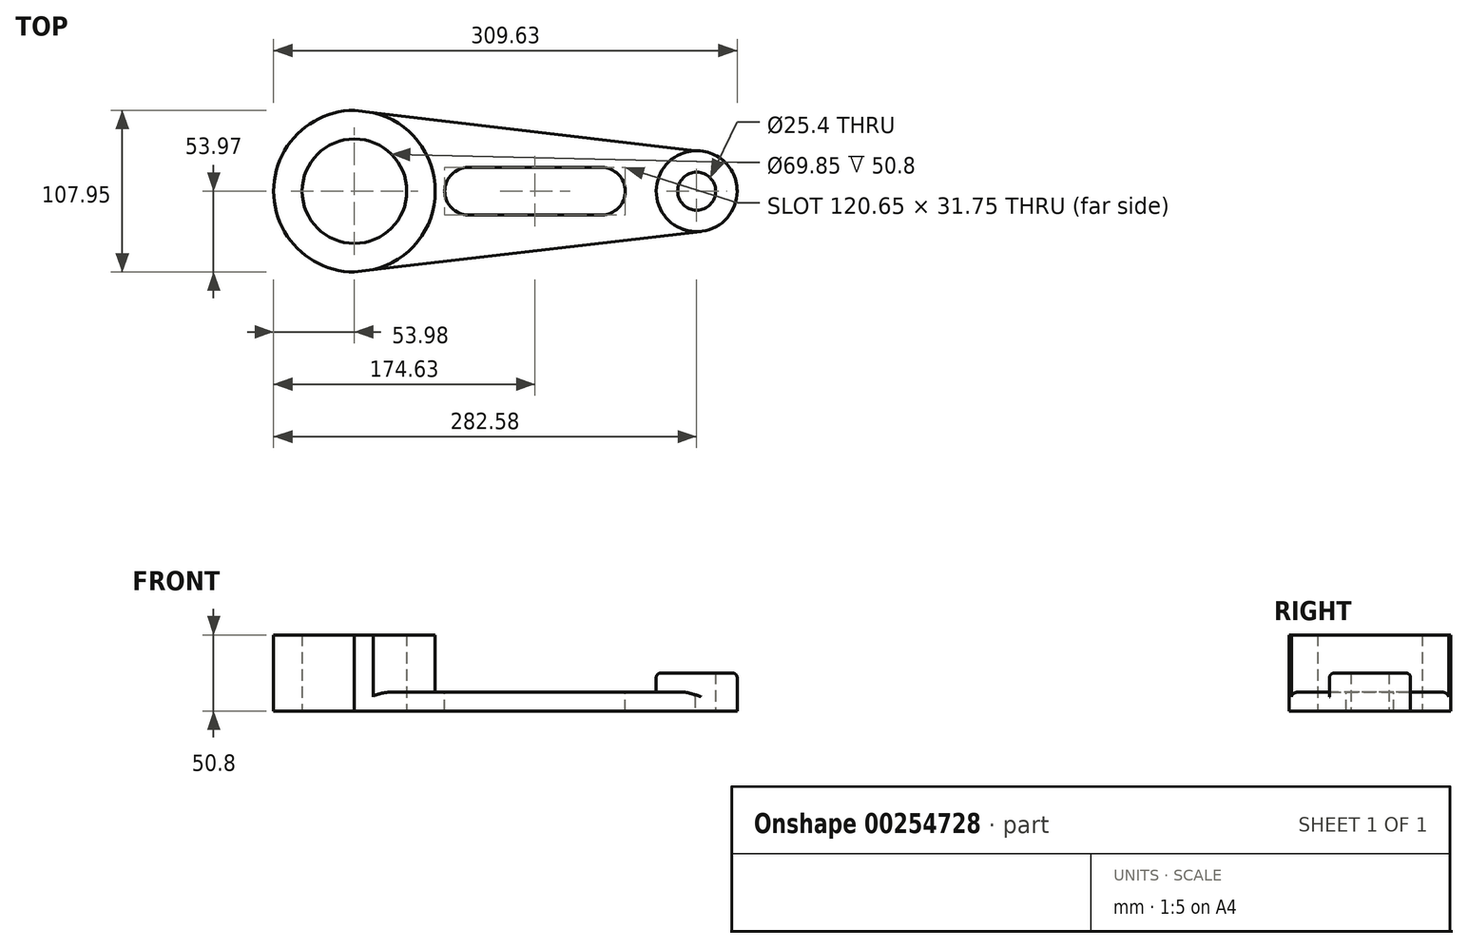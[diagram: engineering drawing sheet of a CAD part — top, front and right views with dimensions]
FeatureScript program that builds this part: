
annotation { "Feature Type Name" : "Feature", "Feature Type Description" : "" }
export const myFeature = defineFeature(function(context is Context, id is Id, definition is map)
    precondition{}
    {
        {
            var Q0;
            Q0=qCreatedBy(makeId("Top.planeOp"),FACE);
            var sketch = newSketch(context, id + "F0", { "sketchPlane" : qUnion([Q0])});
            skCircle(sketch, "E0", {"center": v(152.4, 0) * mm, "radius": 27.05 * mm});
            skCircle(sketch, "E1", {"center": v(152.4, 0) * mm, "radius": 12.7 * mm});
            skCircle(sketch, "E2", {"center": v(-76.2, 0) * mm, "radius": 53.98 * mm});
            skCircle(sketch, "E3", {"center": v(-76.2, 0) * mm, "radius": 34.93 * mm});
            skArc(sketch, "E4", {"start": v(0, 15.88) * mm, "mid": v(-15.88, 0) * mm, "end": v(0, -15.88) * mm});
            skArc(sketch, "E5", {"start": v(88.9, -15.88) * mm, "mid": v(104.78, 0) * mm, "end": v(88.9, 15.88) * mm});
            skLineSegment(sketch, "E6", {"start": v(0, 15.88) * mm, "end": v(88.9, 15.88) * mm});
            skLineSegment(sketch, "E7", {"start": v(0, -15.88) * mm, "end": v(88.9, -15.88) * mm});
            skLineSegment(sketch, "E8", {"start": v(-76.15, 53.97) * mm, "end": v(151.22, 27.03) * mm});
            skLineSegment(sketch, "E9", {"start": v(-76.23, -53.97) * mm, "end": v(155.54, -26.87) * mm});
            skSolve(sketch);
        }
        {
            var Q0;
            Q0=makeQuery(id+"F0.imprint","IMPRINT",FACE,{"disambiguationData":[TD([[makeQuery(id+"F0.imprint","IMPRINT",EDGE,{"derivedFrom":sQuery(id+"F0.wireOp",EDGE,"E3")}),-1.0]])]});
            extrude(context, id + "F1", {"entities" : qUnion([Q0]), "depth" : 50.8 * mm});
        }
        {
            var Q0;
            Q0=makeQuery(id+"F0.imprint","IMPRINT",FACE,{"disambiguationData":[TD([[makeQuery(id+"F0.imprint","IMPRINT",EDGE,{"derivedFrom":sQuery(id+"F0.wireOp",EDGE,"E3")}),1.0]])]});
            extrude(context, id + "F2", {"entities" : qUnion([Q0]), "operationType" : NewBodyOperationType.ADD, "depth" : 50.8 * mm});
        }
        {
            var Q0;
            Q0=makeQuery(id+"F0.imprint","IMPRINT",FACE,{"disambiguationData":[TD([[makeQuery(id+"F0.imprint","IMPRINT",EDGE,{"derivedFrom":sQuery(id+"F0.wireOp",EDGE,"E4")}),-1.0]])]});
            extrude(context, id + "F3", {"entities" : qUnion([Q0]), "operationType" : NewBodyOperationType.ADD, "depth" : 12.7 * mm});
        }
        {
            var Q0;
            Q0=makeQuery(id+"F0.imprint","IMPRINT",FACE,{"disambiguationData":[TD([[makeQuery(id+"F0.imprint","IMPRINT",EDGE,{"derivedFrom":sQuery(id+"F0.wireOp",EDGE,"E4")}),1.0]])]});
            extrude(context, id + "F4", {"entities" : qUnion([Q0]), "operationType" : NewBodyOperationType.ADD, "endBound" : BoundingType.THROUGH_ALL, "depth" : 25.4 * mm});
        }
        {
            var Q0;
            Q0=makeQuery(id+"F4.opExtrude","CAP_FACE",FACE,{"disambiguationData":[OSD([sQuery(id+"F0.wireOp",EDGE,"E4"),sQuery(id+"F0.wireOp",EDGE,"E5"),sQuery(id+"F0.wireOp",EDGE,"E6"),sQuery(id+"F0.wireOp",EDGE,"E7")])],"isStart":false});
            extrude(context, id + "F5", {"entities" : qUnion([Q0]), "operationType" : NewBodyOperationType.REMOVE, "endBound" : BoundingType.THROUGH_ALL, "oppositeDirection" : true, "depth" : 25.4 * mm});
        }
        {
            var Q0;
            Q0=makeQuery(id+"F0.imprint","IMPRINT",FACE,{"disambiguationData":[TD([[makeQuery(id+"F0.imprint","IMPRINT",EDGE,{"derivedFrom":sQuery(id+"F0.wireOp",EDGE,"E1")}),-1.0]])]});
            extrude(context, id + "F6", {"entities" : qUnion([Q0]), "operationType" : NewBodyOperationType.ADD, "depth" : 25.4 * mm});
        }
        {
            var Q0;
            {var subQ0=sQuery(id+"F0.wireOp",EDGE,"E2");Q0=makeQuery(id+"F1.opExtrude","CAP_EDGE",EDGE,{"disambiguationData":[OSD([subQ0]),TDD([makeQuery(id+"F0.imprint","IMPRINT",EDGE,{"disambiguationData":[TD([[makeQuery(id+"F0.imprint","INTERSECT",VERTEX,{"disambiguationData":[OD(0.0)],"derivedFrom":[subQ0,sQuery(id+"F0.wireOp",EDGE,"E8")]}),-1.0]])],"derivedFrom":subQ0})])],"isStart":false});}
            var Q1;
            Q1=makeQuery(id+"F3.opExtrude","CAP_EDGE",EDGE,{"disambiguationData":[OSD([sQuery(id+"F0.wireOp",EDGE,"E9")])],"isStart":false});
            var Q2;
            Q2=makeQuery(id+"F1.opExtrude","CAP_EDGE",EDGE,{"disambiguationData":[OSD([sQuery(id+"F0.wireOp",EDGE,"E9")])],"isStart":false});
            var Q3;
            Q3=makeQuery(id+"F6.opExtrude","CAP_EDGE",EDGE,{"disambiguationData":[OSD([sQuery(id+"F0.wireOp",EDGE,"E0")])],"isStart":false});
            var Q4;
            Q4=makeQuery(id+"F3.opExtrude","CAP_EDGE",EDGE,{"disambiguationData":[OSD([sQuery(id+"F0.wireOp",EDGE,"E8")])],"isStart":false});
            var Q5;
            Q5=makeQuery(id+"F1.opExtrude","CAP_EDGE",EDGE,{"disambiguationData":[OSD([sQuery(id+"F0.wireOp",EDGE,"E8")])],"isStart":false});
            var Q6;
            {var subQ0=sQuery(id+"F0.wireOp",EDGE,"E2");Q6=makeQuery(id+"F1.opExtrude","CAP_EDGE",EDGE,{"disambiguationData":[OSD([subQ0]),TDD([makeQuery(id+"F0.imprint","IMPRINT",EDGE,{"disambiguationData":[TD([[makeQuery(id+"F0.imprint","INTERSECT",VERTEX,{"disambiguationData":[OD(1.0)],"derivedFrom":[subQ0,sQuery(id+"F0.wireOp",EDGE,"E8")]}),1.0]])],"derivedFrom":subQ0})])],"isStart":false});}
            var Q7;
            Q7=makeQuery(id+"F3.opExtrude","CAP_EDGE",EDGE,{"disambiguationData":[OSD([sQuery(id+"F0.wireOp",EDGE,"E7")])],"isStart":false});
            var Q8;
            Q8=makeQuery(id+"F3.opExtrude","CAP_EDGE",EDGE,{"disambiguationData":[OSD([sQuery(id+"F0.wireOp",EDGE,"E4")])],"isStart":false});
            var Q9;
            Q9=makeQuery(id+"F3.opExtrude","CAP_EDGE",EDGE,{"disambiguationData":[OSD([sQuery(id+"F0.wireOp",EDGE,"E6")])],"isStart":false});
            var Q10;
            Q10=makeQuery(id+"F3.opExtrude","CAP_EDGE",EDGE,{"disambiguationData":[OSD([sQuery(id+"F0.wireOp",EDGE,"E5")])],"isStart":false});
            fillet(context, id + "F7", {"entities" : qUnion([Q0, Q1, Q2, Q3, Q4, Q5, Q6, Q7, Q8, Q9, Q10]), "radius" : 3.17 * mm, "tangentPropagation" : true, "allowEdgeOverflow" : false});
        }
        {
            var Q0;
            {var subQ0=sQuery(id+"F0.wireOp",EDGE,"E3");Q0=makeQuery(id+"F2.boolean.opBoolean","MERGE",FACE,{"derivedFrom":[makeQuery(id+"F1.opExtrude","CAP_FACE",FACE,{"disambiguationData":[OSD([sQuery(id+"F0.wireOp",EDGE,"E2"),subQ0,sQuery(id+"F0.wireOp",EDGE,"E8"),sQuery(id+"F0.wireOp",EDGE,"E9")])],"isStart":false}),makeQuery(id+"F2.opExtrude","CAP_FACE",FACE,{"disambiguationData":[OSD([subQ0])],"isStart":false})]});}
            extrude(context, id + "F8", {"entities" : qUnion([Q0]), "operationType" : NewBodyOperationType.REMOVE, "oppositeDirection" : true, "depth" : 50.8 * mm});
        }
        {
            var Q0;
            Q0=makeQuery(id+"F0.imprint","IMPRINT",FACE,{"disambiguationData":[TD([[makeQuery(id+"F0.imprint","IMPRINT",EDGE,{"derivedFrom":sQuery(id+"F0.wireOp",EDGE,"E3")}),-1.0]])]});
            extrude(context, id + "F9", {"entities" : qUnion([Q0]), "operationType" : NewBodyOperationType.ADD, "depth" : 50.8 * mm});
        }
        {
            var Q0;
            Q0=makeQuery(id+"F0.imprint","IMPRINT",FACE,{"disambiguationData":[TD([[makeQuery(id+"F0.imprint","IMPRINT",EDGE,{"derivedFrom":sQuery(id+"F0.wireOp",EDGE,"E3")}),1.0]])]});
            extrude(context, id + "F10", {"entities" : qUnion([Q0]), "operationType" : NewBodyOperationType.REMOVE, "endBound" : BoundingType.THROUGH_ALL, "oppositeDirection" : true, "depth" : 25.4 * mm});
        }
    });
